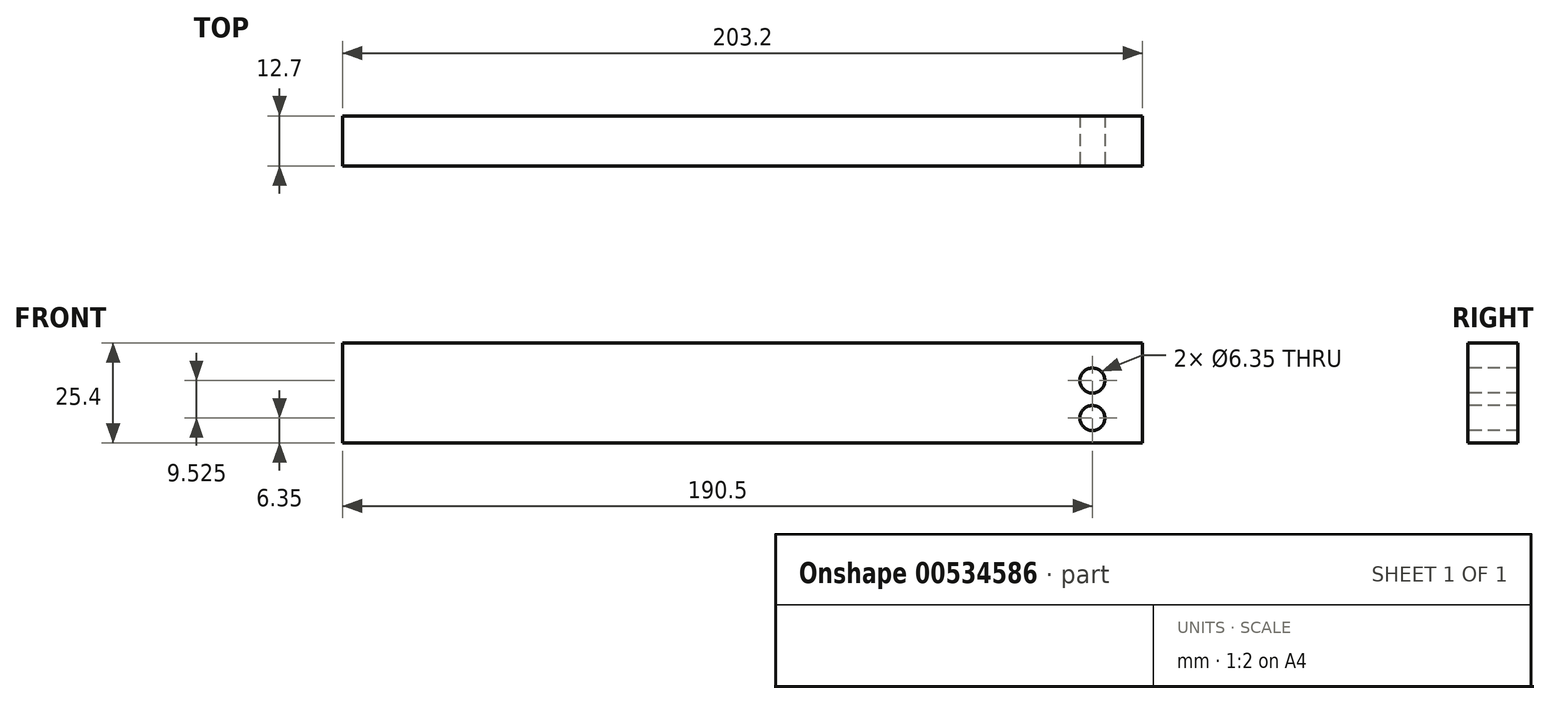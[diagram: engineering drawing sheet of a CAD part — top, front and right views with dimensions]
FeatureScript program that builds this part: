
annotation { "Feature Type Name" : "Feature", "Feature Type Description" : "" }
export const myFeature = defineFeature(function(context is Context, id is Id, definition is map)
    precondition{}
    {
        {
            var Q0;
            Q0=qCreatedBy(makeId("Front.planeOp"),FACE);
            var sketch = newSketch(context, id + "F0", { "sketchPlane" : qUnion([Q0])});
            skLineSegment(sketch, "E0.bottom", {"start": v(0, 0) * mm, "end": v(203.2, 0) * mm});
            skLineSegment(sketch, "E0.top", {"start": v(0, 25.4) * mm, "end": v(203.2, 25.4) * mm});
            skLineSegment(sketch, "E0.left", {"start": v(0, 0) * mm, "end": v(0, 25.4) * mm});
            skLineSegment(sketch, "E0.right", {"start": v(203.2, 0) * mm, "end": v(203.2, 25.4) * mm});
            skSolve(sketch);
        }
        {
            var Q0;
            Q0=makeQuery(id+"F0.imprint","IMPRINT",FACE,{"disambiguationData":[TD([[makeQuery(id+"F0.imprint","IMPRINT",EDGE,{"derivedFrom":sQuery(id+"F0.wireOp",EDGE,"E0.bottom")}),1.0]])]});
            extrude(context, id + "F1", {"entities" : qUnion([Q0]), "depth" : 12.7 * mm, "offsetDistance" : 25.4 * mm});
        }
        {
            var Q0;
            Q0=makeQuery(id+"F1.opExtrude","CAP_FACE",FACE,{"disambiguationData":[OSD([sQuery(id+"F0.wireOp",EDGE,"E0.bottom"),sQuery(id+"F0.wireOp",EDGE,"E0.top"),sQuery(id+"F0.wireOp",EDGE,"E0.left"),sQuery(id+"F0.wireOp",EDGE,"E0.right")])],"isStart":false});
            var sketch = newSketch(context, id + "F2", { "sketchPlane" : qUnion([Q0])});
            skLineSegment(sketch, "E1", {"start": v(203.2, 0) * mm, "end": v(190.5, 0) * mm});
            skLineSegment(sketch, "E2", {"start": v(190.5, 0) * mm, "end": v(190.5, 6.35) * mm});
            skLineSegment(sketch, "E3", {"start": v(190.5, 6.35) * mm, "end": v(190.5, 15.88) * mm});
            skCircle(sketch, "E4", {"center": v(190.5, 6.35) * mm, "radius": 3.18 * mm});
            skCircle(sketch, "E5", {"center": v(190.5, 15.88) * mm, "radius": 3.18 * mm});
            skSolve(sketch);
        }
        {
            var Q0;
            Q0=makeQuery(id+"F2.imprint","IMPRINT",FACE,{"disambiguationData":[TD([[makeQuery(id+"F2.imprint","IMPRINT",EDGE,{"derivedFrom":sQuery(id+"F2.wireOp",EDGE,"E5")}),1.0]])]});
            var Q1;
            {var subQ0=sQuery(id+"F2.wireOp",EDGE,"E3");var subQ1=sQuery(id+"F2.wireOp",EDGE,"E2");var subQ2=makeQuery(id+"F2.imprint","INTERSECT",VERTEX,{"derivedFrom":[subQ1,subQ0]});Q1=makeQuery(id+"F2.imprint","IMPRINT",FACE,{"disambiguationData":[TD([[makeQuery(id+"F2.imprint","IMPRINT",EDGE,{"disambiguationData":[TD([[subQ2,1.0]])],"derivedFrom":subQ1}),-1.0]])]});}
            var Q2;
            {var subQ0=sQuery(id+"F2.wireOp",EDGE,"E3");var subQ1=sQuery(id+"F2.wireOp",EDGE,"E2");var subQ2=makeQuery(id+"F2.imprint","INTERSECT",VERTEX,{"derivedFrom":[subQ1,subQ0]});Q2=makeQuery(id+"F2.imprint","IMPRINT",FACE,{"disambiguationData":[TD([[makeQuery(id+"F2.imprint","IMPRINT",EDGE,{"disambiguationData":[TD([[subQ2,1.0]])],"derivedFrom":subQ1}),1.0]])]});}
            extrude(context, id + "F3", {"entities" : qUnion([Q0, Q1, Q2]), "operationType" : NewBodyOperationType.REMOVE, "oppositeDirection" : true, "depth" : 25.4 * mm, "offsetDistance" : 25.4 * mm});
        }
    });
